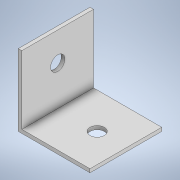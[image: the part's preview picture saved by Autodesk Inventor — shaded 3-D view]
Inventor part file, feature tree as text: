
AUTODESK INVENTOR PART (.ipt)
format: ipt  version: 2020.2 (Build 242310000, 310)  size: 114,176 bytes
history: native  units: in
note: dims shown in document units (in); Inventor stores cm internally (conversion verified against a paired STEP export)
features: extrude x4, sketch x4
ambient origin geometry x8: Origin, YZ Plane, XZ Plane, XY Plane, X Axis, Y Axis, Z Axis, Center Point
bodies: Solid1 (feature_tree)
feature tree (8):
  extrude  "Extrusion1"  Depth=0.7874in
  extrude  "Extrusion2"  Depth=0.0394in
  extrude  "Extrusion3"  Depth=0.748in
  extrude  "Extrusion4"  Depth=0.3937in TaperAngle=0.0deg
  sketch  "Sketch1"  dims[d0=0.7874in d1=0.7874in]
  sketch  "Sketch2"  dims[d2=0.0394in d3=0.0in d4=0.0394in]
  sketch  "Sketch3"  dims[d5=0.748in d6=0.0in d7=0.1575in]
  sketch  "Sketch4"  dims[d8=0.3937in d9=0.0in d10=0.3937in d11=0.0in]
